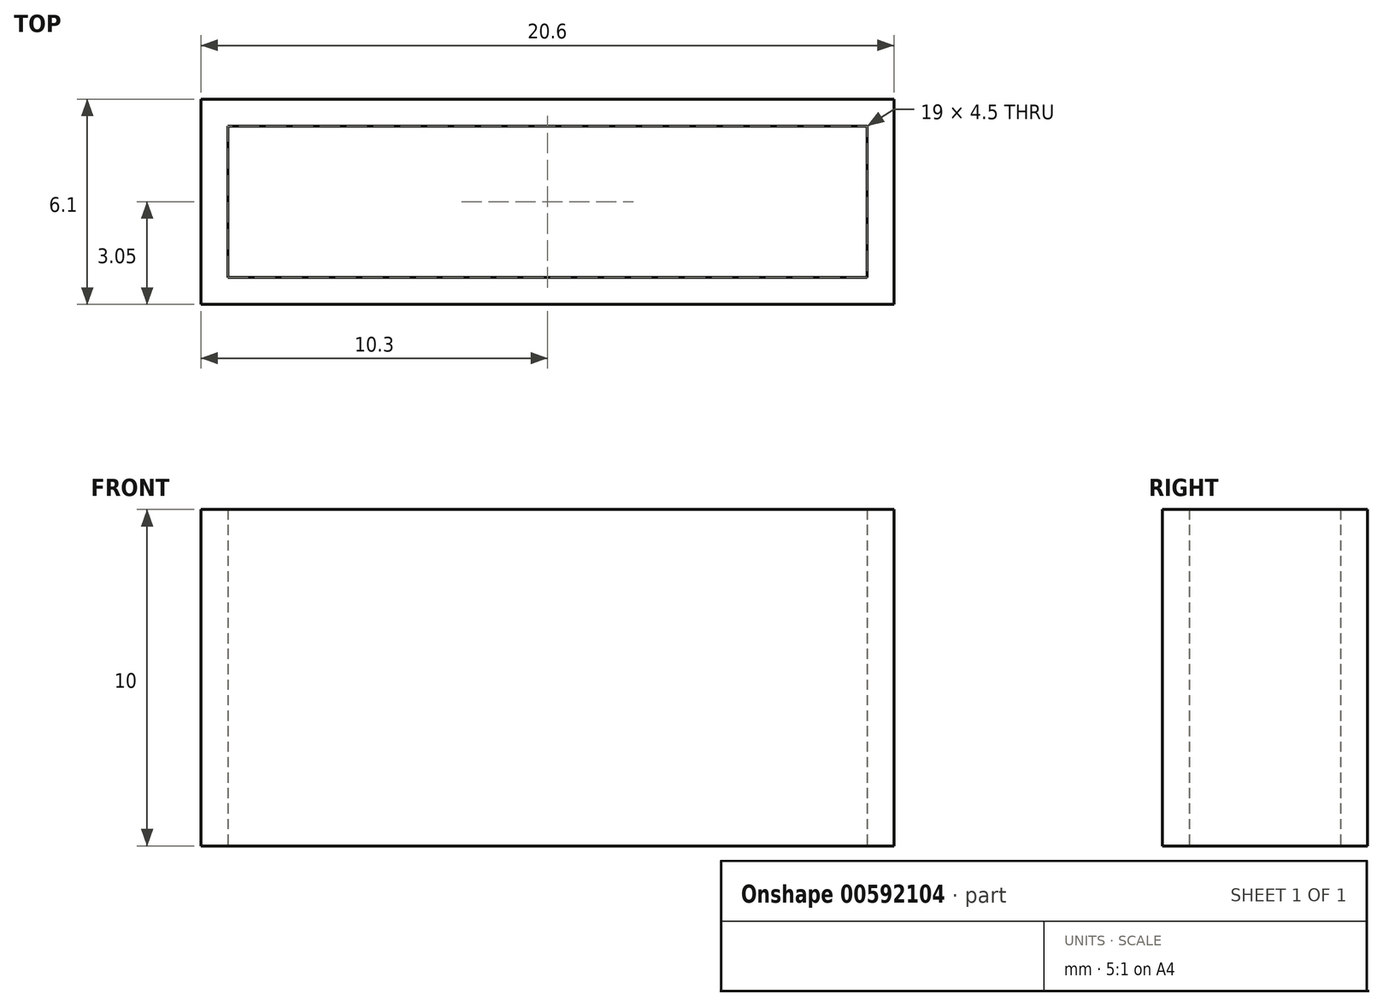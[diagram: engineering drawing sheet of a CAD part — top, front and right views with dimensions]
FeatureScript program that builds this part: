
annotation { "Feature Type Name" : "Feature", "Feature Type Description" : "" }
export const myFeature = defineFeature(function(context is Context, id is Id, definition is map)
    precondition{}
    {
        {
            var Q0;
            Q0=qCreatedBy(makeId("Top.planeOp"),FACE);
            var sketch = newSketch(context, id + "F0", { "sketchPlane" : qUnion([Q0])});
            skLineSegment(sketch, "E0.bottom", {"start": v(10.3, -3.05) * mm, "end": v(-10.3, -3.05) * mm});
            skLineSegment(sketch, "E0.top", {"start": v(10.3, 3.05) * mm, "end": v(-10.3, 3.05) * mm});
            skLineSegment(sketch, "E0.left", {"start": v(10.3, -3.05) * mm, "end": v(10.3, 3.05) * mm});
            skLineSegment(sketch, "E0.right", {"start": v(-10.3, -3.05) * mm, "end": v(-10.3, 3.05) * mm});
            skPoint(sketch, "E0.middle", {"position": v(0, 0) * mm});
            skLineSegment(sketch, "E1.bottom", {"start": v(9.5, -2.25) * mm, "end": v(-9.5, -2.25) * mm});
            skLineSegment(sketch, "E1.top", {"start": v(9.5, 2.25) * mm, "end": v(-9.5, 2.25) * mm});
            skLineSegment(sketch, "E1.left", {"start": v(9.5, -2.25) * mm, "end": v(9.5, 2.25) * mm});
            skLineSegment(sketch, "E1.right", {"start": v(-9.5, -2.25) * mm, "end": v(-9.5, 2.25) * mm});
            skSolve(sketch);
        }
        {
            var Q0;
            Q0=makeQuery(id+"F0.imprint","IMPRINT",FACE,{"disambiguationData":[TD([[makeQuery(id+"F0.imprint","IMPRINT",EDGE,{"derivedFrom":sQuery(id+"F0.wireOp",EDGE,"E0.bottom")}),-1.0]])]});
            extrude(context, id + "F1", {"entities" : qUnion([Q0]), "depth" : 10 * mm, "offsetDistance" : 25 * mm});
        }
    });
